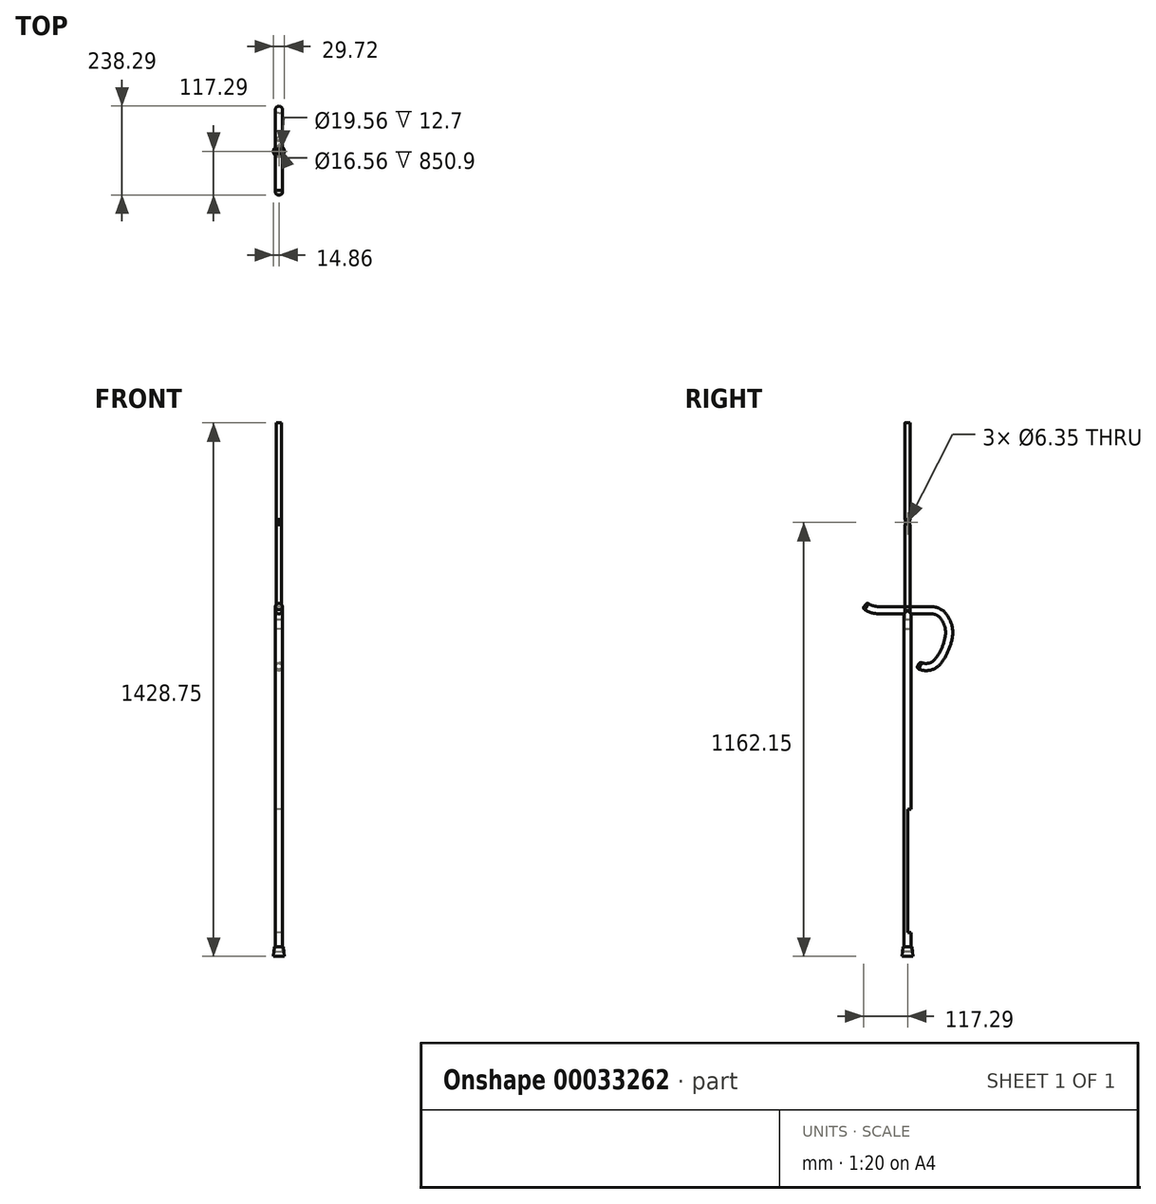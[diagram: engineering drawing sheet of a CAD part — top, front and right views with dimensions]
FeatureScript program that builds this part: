
annotation { "Feature Type Name" : "Feature", "Feature Type Description" : "" }
export const myFeature = defineFeature(function(context is Context, id is Id, definition is map)
    precondition{}
    {
        {
            var Q0;
            Q0=qCreatedBy(makeId("Top.planeOp"),FACE);
            var sketch = newSketch(context, id + "F0", { "sketchPlane" : qUnion([Q0])});
            skCircle(sketch, "E0", {"center": v(0, 0) * mm, "radius": 8.28 * mm});
            skCircle(sketch, "E1", {"center": v(0, 0) * mm, "radius": 9.53 * mm});
            skSolve(sketch);
        }
        {
            var Q0;
            Q0 = qSketchRegion(id + "F0", true);
            extrude(context, id + "F1", {"entities" : qUnion([Q0]), "oppositeDirection" : true, "depth" : 889 * mm});
        }
        {
            var Q0;
            Q0=makeQuery(id+"F1.opExtrude","CAP_FACE",FACE,{"disambiguationData":[OSD([sQuery(id+"F0.wireOp",EDGE,"E0"),sQuery(id+"F0.wireOp",EDGE,"E1")])],"isStart":false});
            cPlane(context, id + "F2", {"entities" : qUnion([Q0]), "cplaneType" : CPlaneType.OFFSET, "offset" : 12.7 * mm, "oppositeDirection" : true, "width" : 152.4 * mm, "height" : 152.4 * mm});
        }
        {
            var Q0;
            Q0=qCreatedBy(id+"F2.planeOp",FACE);
            cPlane(context, id + "F3", {"entities" : qUnion([Q0]), "cplaneType" : CPlaneType.OFFSET, "offset" : 25.4 * mm, "width" : 152.4 * mm, "height" : 152.4 * mm});
        }
        {
            var Q0;
            Q0=qCreatedBy(id+"F2.planeOp",FACE);
            var sketch = newSketch(context, id + "F4", { "sketchPlane" : qUnion([Q0])});
            skCircle(sketch, "E2", {"center": v(0, 0) * mm, "radius": 9.78 * mm, "construction": true});
            skCircle(sketch, "E3", {"center": v(0, 0) * mm, "radius": 12.32 * mm});
            skSolve(sketch);
        }
        {
            var Q0;
            Q0=qCreatedBy(id+"F3.planeOp",FACE);
            var sketch = newSketch(context, id + "F5", { "sketchPlane" : qUnion([Q0])});
            skCircle(sketch, "E4", {"center": v(0, 0) * mm, "radius": 14.86 * mm});
            skSolve(sketch);
        }
        {
            var Q1;
            Q1 = qSketchRegion(id + "F4", true);
            var Q2;
            Q2 = qSketchRegion(id + "F5", true);
            loft(context, id + "F6", {"sheetProfilesArray" : [{ "sheetProfileEntities" : qUnion([Q1]) }, { "sheetProfileEntities" : qUnion([Q2]) }]});
        }
        {
            var Q0;
            Q0=makeQuery(id+"F4.imprint","IMPRINT",FACE,{"disambiguationData":[TD([[makeQuery(id+"F4.imprint","IMPRINT",EDGE,{"derivedFrom":sQuery(id+"F4.wireOp",EDGE,"E3")}),1.0]])]});
            var sketch = newSketch(context, id + "F7", { "sketchPlane" : qUnion([Q0])});
            skCircle(sketch, "E5", {"center": v(0, 0) * mm, "radius": 9.78 * mm});
            skSolve(sketch);
        }
        {
            var Q0;
            Q0 = qSketchRegion(id + "F7", true);
            extrude(context, id + "F8", {"entities" : qUnion([Q0]), "operationType" : NewBodyOperationType.REMOVE, "depth" : 12.7 * mm});
        }
        {
            var Q0;
            Q0=qCreatedBy(makeId("Top.planeOp"),FACE);
            var sketch = newSketch(context, id + "F9", { "sketchPlane" : qUnion([Q0])});
            skCircle(sketch, "E6", {"center": v(0, 0) * mm, "radius": 9.53 * mm});
            skCircle(sketch, "E7", {"center": v(0, 0) * mm, "radius": 8.28 * mm});
            skSolve(sketch);
        }
        {
            var Q0;
            Q0=makeQuery(id+"F9.imprint","IMPRINT",FACE,{"disambiguationData":[TD([[makeQuery(id+"F9.imprint","IMPRINT",EDGE,{"derivedFrom":sQuery(id+"F9.wireOp",EDGE,"E7")}),1.0]])]});
            var Q1;
            Q1=sQuery(id+"F9.wireOp",EDGE,"E7");
            extrude(context, id + "F10", {"entities" : qUnion([Q0]), "surfaceEntities" : qUnion([Q1]), "oppositeDirection" : true, "depth" : 25.4 * mm});
        }
        {
            var Q0;
            Q0=makeQuery(id+"F9.imprint","IMPRINT",FACE,{"disambiguationData":[TD([[makeQuery(id+"F9.imprint","IMPRINT",EDGE,{"derivedFrom":sQuery(id+"F9.wireOp",EDGE,"E6")}),1.0]])]});
            var sketch = newSketch(context, id + "F11", { "sketchPlane" : qUnion([Q0])});
            skCircle(sketch, "E8", {"center": v(0, 0) * mm, "radius": 9.53 * mm});
            skSolve(sketch);
        }
        {
            var Q0;
            Q0 = qSketchRegion(id + "F11", true);
            extrude(context, id + "F12", {"entities" : qUnion([Q0]), "operationType" : NewBodyOperationType.ADD, "depth" : 25.4 * mm});
        }
        {
            var Q0;
            Q0=qCreatedBy(makeId("Front.planeOp"),FACE);
            var sketch = newSketch(context, id + "F13", { "sketchPlane" : qUnion([Q0])});
            skCircle(sketch, "E9", {"center": v(0, 25.4) * mm, "radius": 9.53 * mm});
            skSolve(sketch);
        }
        {
            var Q0;
            Q0=qCreatedBy(makeId("Right.planeOp"),FACE);
            var sketch = newSketch(context, id + "F14", { "sketchPlane" : qUnion([Q0])});
            skLineSegment(sketch, "E10", {"start": v(0, 25.4) * mm, "end": v(-76.2, 25.4) * mm});
            skLineSegment(sketch, "E11", {"start": v(0, 25.4) * mm, "end": v(63.5, 25.4) * mm});
            skArc(sketch, "E12", {"start": v(63.5, 25.4) * mm, "mid": v(81.6, 21.26) * mm, "end": v(96.1, 9.67) * mm});
            skArc(sketch, "E13", {"start": v(-76.2, 25.4) * mm, "mid": v(-96.28, 28.66) * mm, "end": v(-114.3, 38.1) * mm});
            skArc(sketch, "E14", {"start": v(96.1, 9.67) * mm, "mid": v(109.4, -17.4) * mm, "end": v(110.23, -47.56) * mm});
            skArc(sketch, "E15", {"start": v(110.23, -47.56) * mm, "mid": v(99.8, -80.86) * mm, "end": v(81.96, -110.85) * mm});
            skArc(sketch, "E16", {"start": v(81.96, -110.85) * mm, "mid": v(57.3, -126.06) * mm, "end": v(28.77, -120.94) * mm});
            skSolve(sketch);
        }
        {
            var Q0;
            Q0=makeQuery(id+"F13.imprint","IMPRINT",FACE,{"disambiguationData":[TD([[makeQuery(id+"F13.imprint","IMPRINT",EDGE,{"derivedFrom":sQuery(id+"F13.wireOp",EDGE,"E9")}),1.0]])]});
            var Q1;
            Q1=sQuery(id+"F14.wireOp",EDGE,"E10");
            var Q2;
            Q2=sQuery(id+"F14.wireOp",EDGE,"E13");
            sweep(context, id + "F15", {"operationType" : NewBodyOperationType.ADD, "profiles" : qUnion([Q0]), "path" : qUnion([Q1, Q2])});
        }
        {
            var Q0;
            Q0 = qSketchRegion(id + "F13", true);
            var Q1;
            Q1=sQuery(id+"F14.wireOp",EDGE,"E11");
            var Q2;
            Q2=sQuery(id+"F14.wireOp",EDGE,"E12");
            var Q3;
            Q3=sQuery(id+"F14.wireOp",EDGE,"E14");
            var Q4;
            Q4=sQuery(id+"F14.wireOp",EDGE,"E15");
            var Q5;
            Q5=sQuery(id+"F14.wireOp",EDGE,"E16");
            sweep(context, id + "F16", {"operationType" : NewBodyOperationType.ADD, "profiles" : qUnion([Q0]), "path" : qUnion([Q1, Q2, Q3, Q4, Q5])});
        }
        {
            var Q0;
            Q0=makeQuery(id+"F15.opSweep","CAP_EDGE",EDGE,{"disambiguationData":[OSD([sQuery(id+"F13.wireOp",EDGE,"E9"),sQuery(id+"F14.wireOp",VERTEX,"E13.end")])],"isStart":false});
            var Q1;
            Q1=makeQuery(id+"F16.opSweep","CAP_EDGE",EDGE,{"disambiguationData":[OSD([sQuery(id+"F13.wireOp",EDGE,"E9"),sQuery(id+"F14.wireOp",VERTEX,"E16.end")])],"isStart":false});
            fillet(context, id + "F17", {"entities" : qUnion([Q0, Q1]), "radius" : 6.35 * mm, "tangentPropagation" : true, "allowEdgeOverflow" : false});
        }
        {
            var Q0;
            Q0=qCreatedBy(makeId("Front.planeOp"),FACE);
            var sketch = newSketch(context, id + "F18", { "sketchPlane" : qUnion([Q0])});
            skLineSegment(sketch, "E17.bottom", {"start": v(9.52, -838.2) * mm, "end": v(-9.52, -838.2) * mm});
            skLineSegment(sketch, "E17.top", {"start": v(9.52, -508) * mm, "end": v(-9.53, -508) * mm});
            skLineSegment(sketch, "E17.left", {"start": v(9.52, -838.2) * mm, "end": v(9.52, -508) * mm});
            skLineSegment(sketch, "E17.right", {"start": v(-9.52, -838.2) * mm, "end": v(-9.53, -508) * mm});
            skSolve(sketch);
        }
        {
            var Q0;
            Q0 = qSketchRegion(id + "F18", true);
            extrude(context, id + "F19", {"entities" : qUnion([Q0]), "operationType" : NewBodyOperationType.REMOVE, "oppositeDirection" : true, "depth" : 25.4 * mm});
        }
        {
            var Q0;
            Q0=qCreatedBy(makeId("Top.planeOp"),FACE);
            var sketch = newSketch(context, id + "F20", { "sketchPlane" : qUnion([Q0])});
            skCircle(sketch, "E18", {"center": v(0, 0) * mm, "radius": 7.01 * mm});
            skSolve(sketch);
        }
        {
            var Q0;
            Q0 = qSketchRegion(id + "F20", true);
            extrude(context, id + "F21", {"entities" : qUnion([Q0]), "depth" : 254 * mm});
        }
        {
            var Q0;
            Q0=makeQuery(id+"F21.opExtrude","CAP_FACE",FACE,{"disambiguationData":[OSD([sQuery(id+"F20.wireOp",EDGE,"E18")])],"isStart":false});
            var sketch = newSketch(context, id + "F22", { "sketchPlane" : qUnion([Q0])});
            skArc(sketch, "E19", {"start": v(3.18, -6.25) * mm, "mid": v(0, 7.01) * mm, "end": v(-3.18, -6.25) * mm});
            skLineSegment(sketch, "E20.left", {"start": v(3.17, -6.25) * mm, "end": v(3.17, 6.25) * mm});
            skLineSegment(sketch, "E20.right", {"start": v(-3.18, -6.25) * mm, "end": v(-3.18, 6.25) * mm});
            skSolve(sketch);
        }
        {
            var Q0;
            Q0 = qSketchRegion(id + "F22", true);
            extrude(context, id + "F23", {"entities" : qUnion([Q0]), "operationType" : NewBodyOperationType.ADD, "depth" : 12.7 * mm});
        }
        {
            var Q0;
            Q0=qCreatedBy(makeId("Right.planeOp"),FACE);
            var sketch = newSketch(context, id + "F24", { "sketchPlane" : qUnion([Q0])});
            skArc(sketch, "E21", {"start": v(6.25, 260.45) * mm, "mid": v(0, 266.7) * mm, "end": v(-6.25, 260.45) * mm});
            skPoint(sketch, "E22", {"position": v(0, 266.7) * mm});
            skPoint(sketch, "E23", {"position": v(-6.25, 260.45) * mm});
            skLineSegment(sketch, "E24", {"start": v(-6.25, 260.45) * mm, "end": v(-6.25, 268.21) * mm});
            skLineSegment(sketch, "E25", {"start": v(-6.25, 268.21) * mm, "end": v(6.25, 268.21) * mm});
            skLineSegment(sketch, "E26", {"start": v(6.25, 268.21) * mm, "end": v(6.25, 260.45) * mm});
            skLineSegment(sketch, "E27", {"start": v(6.25, 260.45) * mm, "end": v(-6.25, 260.45) * mm, "construction": true});
            skCircle(sketch, "E28", {"center": v(0, 260.45) * mm, "radius": 3.18 * mm});
            skSolve(sketch);
        }
        {
            var Q0;
            Q0 = qSketchRegion(id + "F24", true);
            extrude(context, id + "F25", {"entities" : qUnion([Q0]), "operationType" : NewBodyOperationType.REMOVE, "endBound" : BoundingType.SYMMETRIC, "oppositeDirection" : true, "depth" : 25.4 * mm});
        }
        {
            var Q0;
            Q0=qCreatedBy(makeId("Right.planeOp"),FACE);
            var sketch = newSketch(context, id + "F26", { "sketchPlane" : qUnion([Q0])});
            skCircle(sketch, "E29", {"center": v(0, 260.45) * mm, "radius": 2.54 * mm});
            skSolve(sketch);
        }
        {
            var Q0;
            Q0 = qSketchRegion(id + "F26", true);
            extrude(context, id + "F27", {"entities" : qUnion([Q0]), "endBound" : BoundingType.SYMMETRIC, "depth" : 13.97 * mm});
        }
        {
            var Q0;
            Q0=qCreatedBy(makeId("Right.planeOp"),FACE);
            var sketch = newSketch(context, id + "F28", { "sketchPlane" : qUnion([Q0])});
            skLineSegment(sketch, "E30.rect.top", {"start": v(-6.25, 273.05) * mm, "end": v(6.25, 273.05) * mm});
            skLineSegment(sketch, "E30.rect.left", {"start": v(-6.25, 260.45) * mm, "end": v(-6.25, 273.05) * mm});
            skLineSegment(sketch, "E30.rect.right", {"start": v(6.25, 260.45) * mm, "end": v(6.25, 273.05) * mm});
            skPoint(sketch, "E30.rect.middle", {"position": v(0, 266.7) * mm});
            skCircle(sketch, "E31", {"center": v(0, 260.45) * mm, "radius": 6.25 * mm, "construction": true});
            skPoint(sketch, "E32", {"position": v(6.25, 260.45) * mm});
            skCircle(sketch, "E33", {"center": v(0, 260.45) * mm, "radius": 3.18 * mm});
            skPoint(sketch, "E34", {"position": v(0, 254.2) * mm});
            skArc(sketch, "E35", {"start": v(6.25, 260.45) * mm, "mid": v(4.42, 256.03) * mm, "end": v(0, 254.2) * mm});
            skArc(sketch, "E36", {"start": v(-6.25, 260.45) * mm, "mid": v(-4.42, 256.03) * mm, "end": v(0, 254.2) * mm});
            skPoint(sketch, "E37", {"position": v(0, 267.36) * mm});
            skSolve(sketch);
        }
        {
            var Q0;
            Q0 = qSketchRegion(id + "F28", true);
            extrude(context, id + "F29", {"entities" : qUnion([Q0]), "endBound" : BoundingType.SYMMETRIC, "depth" : 5.84 * mm});
        }
        {
            var Q0;
            Q0=makeQuery(id+"F29.opExtrude","SWEPT_FACE",FACE,{"disambiguationData":[OSD([sQuery(id+"F28.wireOp",EDGE,"E30.rect.top")])]});
            var sketch = newSketch(context, id + "F30", { "sketchPlane" : qUnion([Q0])});
            skCircle(sketch, "E38", {"center": v(0, 0) * mm, "radius": 7.01 * mm});
            skSolve(sketch);
        }
        {
            var Q0;
            Q0 = qSketchRegion(id + "F30", true);
            extrude(context, id + "F31", {"entities" : qUnion([Q0]), "operationType" : NewBodyOperationType.ADD, "depth" : 254 * mm, "hasSecondDirection" : true, "secondDirectionOppositeDirection" : true, "secondDirectionDepth" : 5.08 * mm});
        }
    });
